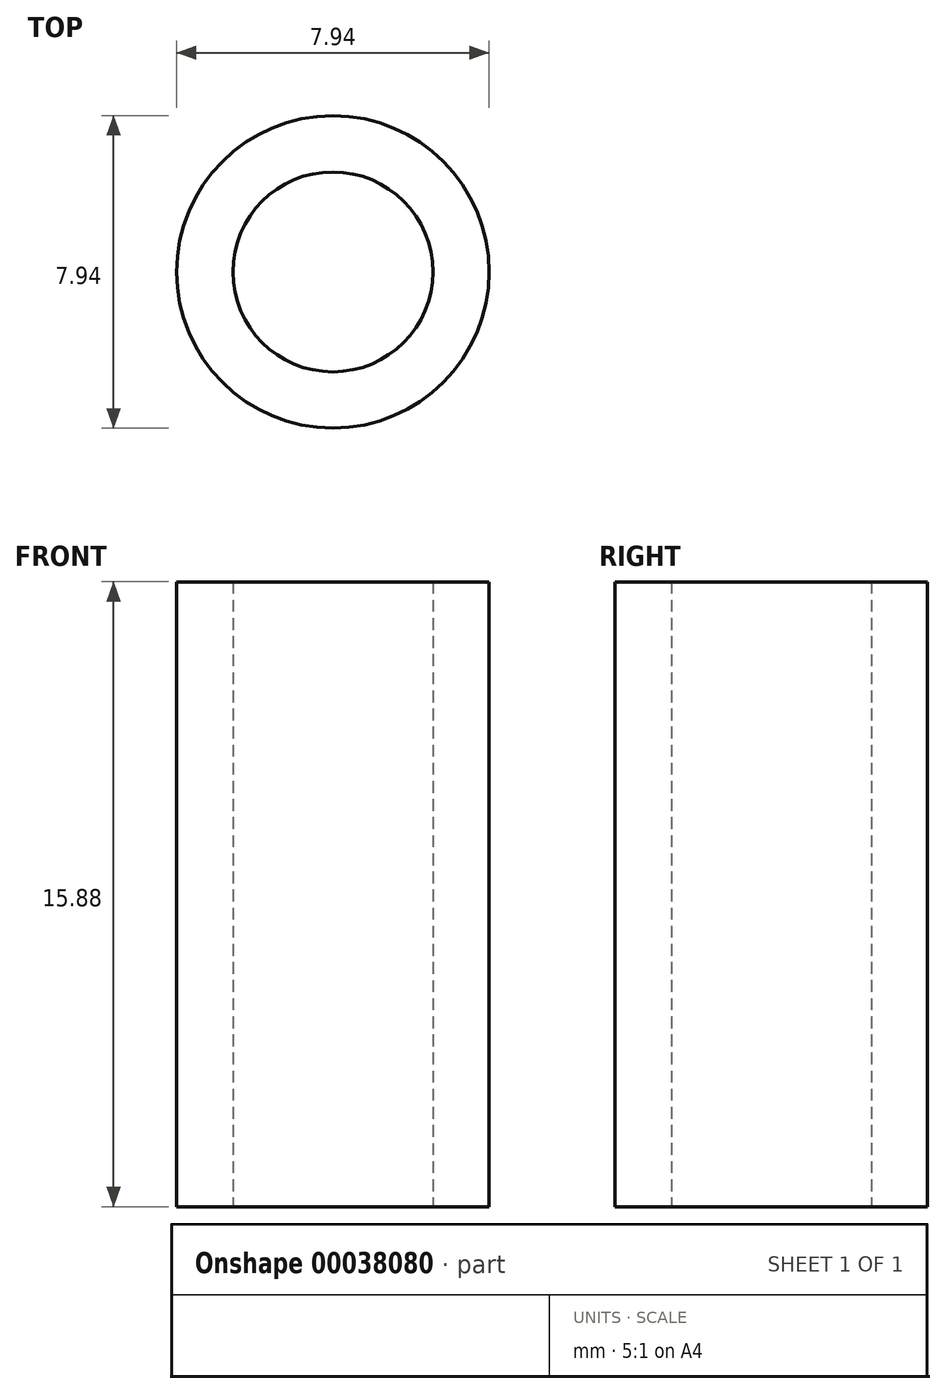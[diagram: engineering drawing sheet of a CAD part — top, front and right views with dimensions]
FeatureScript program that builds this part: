
annotation { "Feature Type Name" : "Feature", "Feature Type Description" : "" }
export const myFeature = defineFeature(function(context is Context, id is Id, definition is map)
    precondition{}
    {
        {
            var Q0;
            Q0=qCreatedBy(makeId("Top.planeOp"),FACE);
            var sketch = newSketch(context, id + "F0", { "sketchPlane" : qUnion([Q0])});
            skCircle(sketch, "E0", {"center": v(0, 0) * mm, "radius": 2.54 * mm});
            skCircle(sketch, "E1", {"center": v(0, 0) * mm, "radius": 3.97 * mm});
            skSolve(sketch);
        }
        {
            var Q0;
            Q0 = qSketchRegion(id + "F0", true);
            extrude(context, id + "F1", {"entities" : qUnion([Q0]), "depth" : 15.88 * mm});
        }
    });
